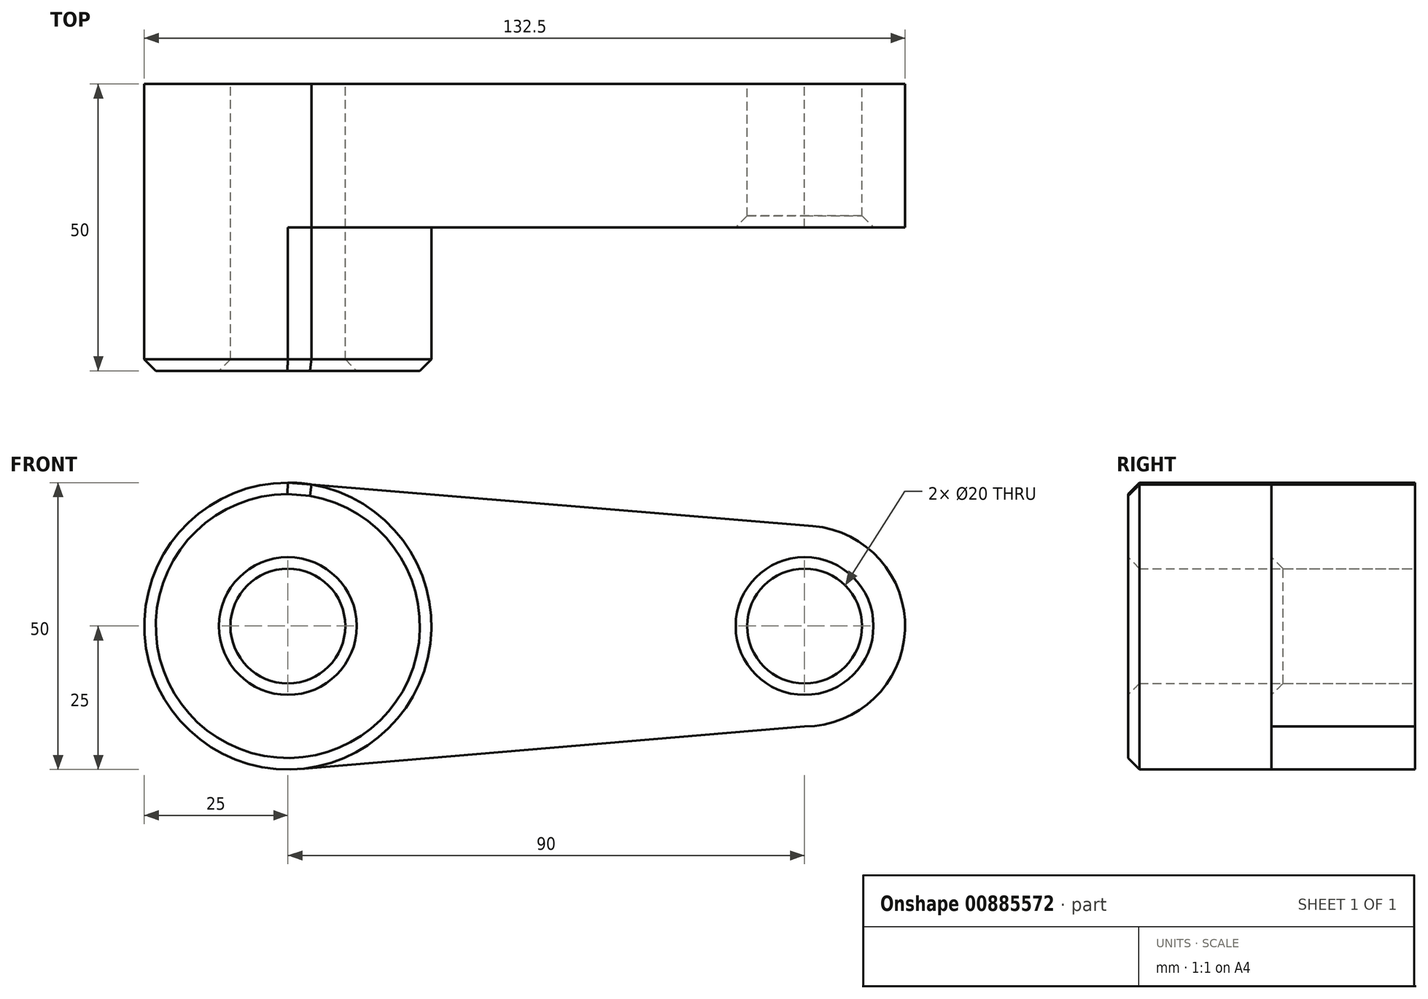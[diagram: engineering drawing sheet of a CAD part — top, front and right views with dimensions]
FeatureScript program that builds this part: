
annotation { "Feature Type Name" : "Feature", "Feature Type Description" : "" }
export const myFeature = defineFeature(function(context is Context, id is Id, definition is map)
    precondition{}
    {
        {
            var Q0;
            Q0=qCreatedBy(makeId("Front.planeOp"),FACE);
            var sketch = newSketch(context, id + "F0", { "sketchPlane" : qUnion([Q0])});
            skCircle(sketch, "E0", {"center": v(0, 0) * mm, "radius": 25 * mm});
            skCircle(sketch, "E1", {"center": v(90, 0) * mm, "radius": 17.5 * mm});
            skLineSegment(sketch, "E2", {"start": v(0, 25) * mm, "end": v(91.44, 17.44) * mm});
            skLineSegment(sketch, "E3", {"start": v(2.1, -24.91) * mm, "end": v(90, -17.5) * mm});
            skCircle(sketch, "E4", {"center": v(0, 0) * mm, "radius": 10 * mm});
            skCircle(sketch, "E5", {"center": v(90, 0) * mm, "radius": 10 * mm});
            skSolve(sketch);
        }
        {
            var Q0;
            Q0 = qSketchRegion(id + "F0", true);
            extrude(context, id + "F1", {"entities" : qUnion([Q0]), "depth" : 25 * mm, "offsetDistance" : 25 * mm});
        }
        {
            var Q0;
            Q0=makeQuery(id+"F0.imprint","IMPRINT",FACE,{"disambiguationData":[TD([[makeQuery(id+"F0.imprint","IMPRINT",EDGE,{"derivedFrom":sQuery(id+"F0.wireOp",EDGE,"E4")}),-1.0]])]});
            extrude(context, id + "F2", {"entities" : qUnion([Q0]), "operationType" : NewBodyOperationType.ADD, "depth" : 50 * mm, "offsetDistance" : 25 * mm});
        }
        {
            var Q0;
            Q0=makeQuery(id+"F2.opExtrude","CAP_FACE",FACE,{"disambiguationData":[OSD([sQuery(id+"F0.wireOp",EDGE,"E0"),sQuery(id+"F0.wireOp",EDGE,"E2"),sQuery(id+"F0.wireOp",EDGE,"E4")])],"isStart":false});
            var Q1;
            Q1=makeQuery(id+"F1.opExtrude","CAP_EDGE",EDGE,{"disambiguationData":[OSD([sQuery(id+"F0.wireOp",EDGE,"E5")])],"isStart":false});
            chamfer(context, id + "F3", {"entities" : qUnion([Q0, Q1]), "width" : 2 * mm, "tangentPropagation" : true});
        }
    });
